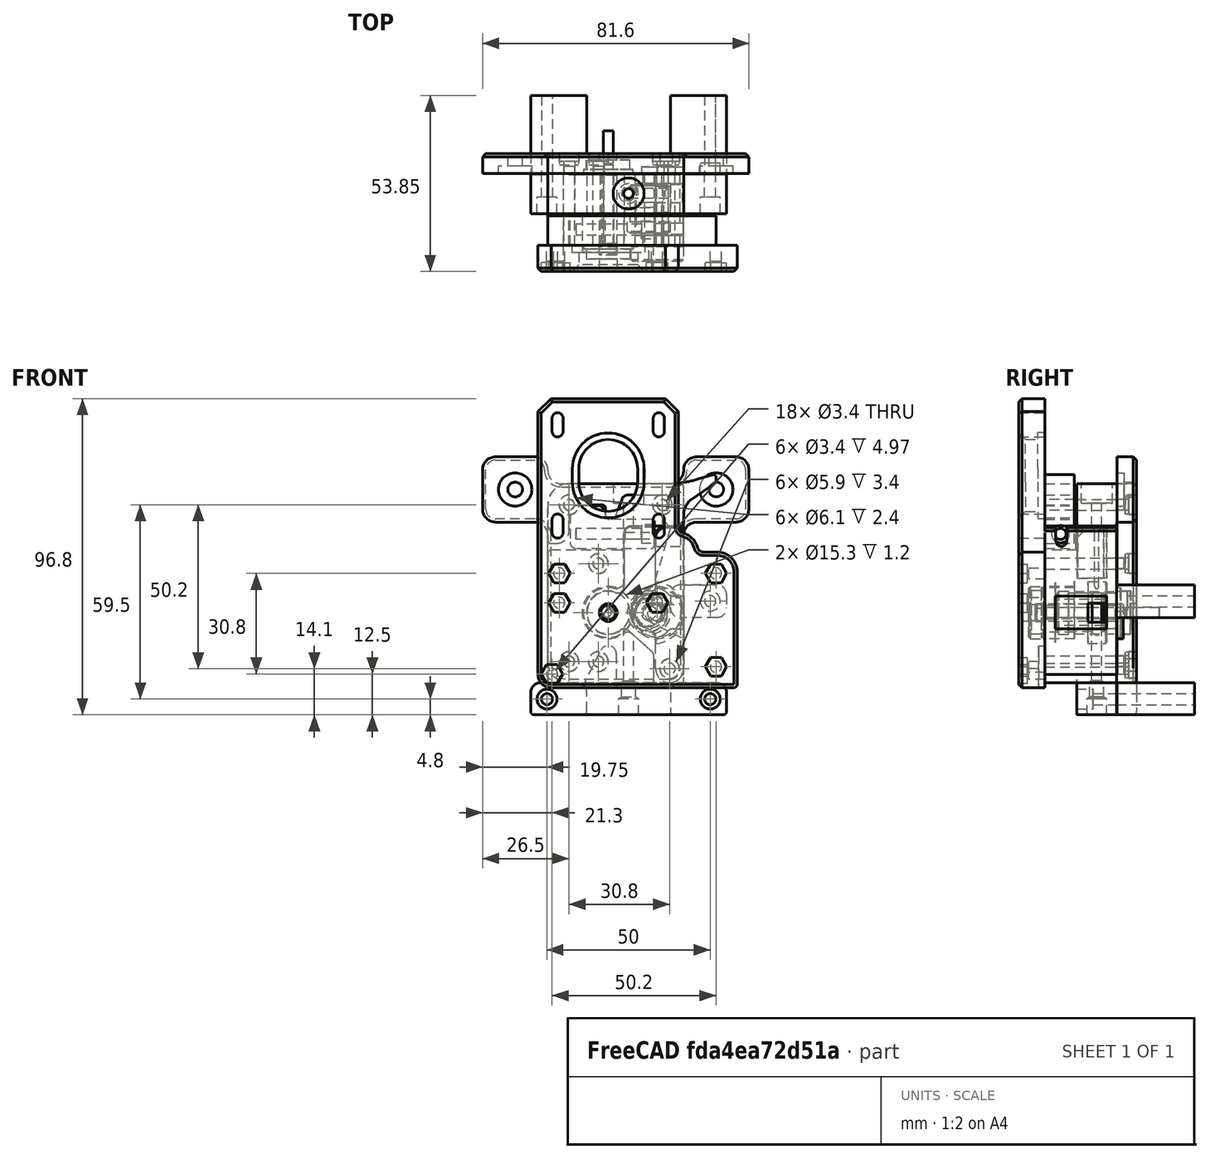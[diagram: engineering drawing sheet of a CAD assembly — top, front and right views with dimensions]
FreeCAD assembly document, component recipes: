
FREECAD ASSEMBLY — COMPONENT RECIPES ("belted_extruder_v0.4")

This assembly document has 4 components, labeled P0..P3 below (a component is one placed body or linked part). 4 of them carry a construction recipe — the FreeCAD feature program that regenerates the part from scratch, quoted from this document or its linked companion documents; the rest are supplied as boundary geometry only. No exploded tour is included for this assembly.
COMPONENT P0 — recipe-attached ("Extruder-BodyLower001", modeled in this document).
Construction recipe (the document's own serialized feature program — sketch geometry with constraints, then the solid features built on it; lengths are millimeters unless a unit is written):

FEATURE [PartDesign::SubShapeBinder] Binder009  label="Body Screw Binders"
  BindCopyOnChange = 0
  BindMode = 0
  ClaimChildren = false
  Context = -> Part005 [Body007.Binder009.]
  Fuse = false
  MakeFace = true
  OffsetFill = false
  OffsetIntersection = false
  OffsetJoinType = 0
  OffsetOpenResult = false
  PartialLoad = false
  Refine = true
  Relative = true
  Support = -> [Sketch014]
  _Version = 2
FEATURE [Sketcher::SketchObject] Sketch036  label="BaseSketch"
  ArcFitTolerance = 1e-06
  AttachmentOffset = pos=(0,0,-22) rot=(0,0,1;0rad)
  AttachmentSupport = -> [XZ_Plane028]
  ExternalGeometry = -> [Binder009]
  FullyConstrained = true
  MakeInternals = false
  MapMode = 5
  Placement = pos=(0,22,-4.9e-15) rot=(1,0,0;1.5708rad)
  sketch-geometry (22):
    g0: LineSegment StartX=-18.5 StartY=39.5 StartZ=0 EndX=-18.5 EndY=-21.5 EndZ=0
    g1: LineSegment [constr] StartX=-18.5 StartY=-21.5 StartZ=0 EndX=14 EndY=-21.5 EndZ=0
    g2: LineSegment StartX=14 StartY=-21.5 StartZ=0 EndX=14 EndY=-12.5 EndZ=0
    g3: ArcOfCircle CenterX=0 CenterY=0 CenterZ=0 NormalX=0 NormalY=0 NormalZ=1 AngleXU=0 Radius=6.5 StartAngle=0.720958 EndAngle=5.56223
    g4: Circle CenterX=-3 CenterY=15 CenterZ=0 NormalX=0 NormalY=0 NormalZ=1 AngleXU=0 Radius=1.7
    g5: Circle CenterX=-3 CenterY=-15 CenterZ=0 NormalX=0 NormalY=0 NormalZ=1 AngleXU=0 Radius=1.7
    g6: LineSegment [constr] StartX=4.88263 StartY=4.29068 StartZ=0 EndX=14 EndY=12.5 EndZ=0
    g7: LineSegment StartX=4.88263 StartY=-4.29068 StartZ=0 EndX=14 EndY=-12.5 EndZ=0
    g8: LineSegment [constr] StartX=14 StartY=12.5 StartZ=0 EndX=14 EndY=-12.5 EndZ=0
    g9: LineSegment [constr] StartX=4.88263 StartY=4.29068 StartZ=0 EndX=4.88263 EndY=-4.29068 EndZ=0
    g10: LineSegment StartX=23.1 StartY=39.5 StartZ=0 EndX=-18.5 EndY=39.5 EndZ=0
    g11: LineSegment StartX=4.88263 StartY=26.5 StartZ=0 EndX=23.1 EndY=26.5 EndZ=0
    g12: LineSegment StartX=23.1 StartY=26.5 StartZ=0 EndX=23.1 EndY=39.5 EndZ=0
    g13: LineSegment StartX=4.88263 StartY=26.5 StartZ=0 EndX=4.88263 EndY=4.29068 EndZ=0
    g14: Circle CenterX=16.6 CenterY=33 CenterZ=0 NormalX=0 NormalY=0 NormalZ=1 AngleXU=0 Radius=1.7
    g15: Circle CenterX=-12 CenterY=33 CenterZ=0 NormalX=0 NormalY=0 NormalZ=1 AngleXU=0 Radius=1.7
    g16: Circle CenterX=-12 CenterY=-15 CenterZ=0 NormalX=0 NormalY=0 NormalZ=1 AngleXU=0 Radius=1.7
    g17: LineSegment StartX=-18.5 StartY=-21.5 StartZ=0 EndX=-23.75 EndY=-21.5 EndZ=0
    g18: LineSegment StartX=-23.75 StartY=-21.5 StartZ=0 EndX=-23.75 EndY=-31.3 EndZ=0
    g19: LineSegment StartX=-23.75 StartY=-31.3 StartZ=0 EndX=36.25 EndY=-31.3 EndZ=0
    g20: LineSegment StartX=36.25 StartY=-31.3 StartZ=0 EndX=36.25 EndY=-21.5 EndZ=0
    g21: LineSegment StartX=36.25 StartY=-21.5 StartZ=0 EndX=14 EndY=-21.5 EndZ=0
  constraints (58):
    c: Coincident(g0,g1)
    c: Coincident(g1,g2)
    c: Coincident(g10,g0)
    c: Vertical(g0)
    c: Vertical(g2)
    c: Horizontal(g1)
    c: DistanceX(g0,g-3) = 6.5
    c: DistanceY(g0,g-4) = 6.5
    c: Coincident(g3,g-1)
    c: Diameter(g3) = 13
    c: DistanceY(g-3,g0) = 6.5
    c: Coincident(g4,g-5)
    c: Equal(g4,g-5)
    c: Coincident(g5,g-6)
    c: Equal(g5,g-6)
    c: DistanceY(g7,g6) = 25
    c: Symmetric(g6,g7,g-1)
    c: PointOnObject(g2,g7)
    c: Coincident(g8,g6)
    c: Coincident(g8,g2)
    c: Vertical(g8)
    c: Coincident(g7,g3)
    c: Coincident(g6,g3)
    c: Angle(g7,g6) = 1.46608
    c: Coincident(g9,g3)
    c: Coincident(g9,g3)
    c: Vertical(g9)
    c: Horizontal(g10)
    c: Horizontal(g11)
    c: Coincident(g12,g11)
    c: Vertical(g12)
    c: DistanceX(g3,g1) = 14
    c: Coincident(g13,g11)
    c: Vertical(g13)
    c: DistanceX(g-7,g12) = 6.5
    c: Coincident(g10,g12)
    c: DistanceY(g11,g-7) = 6.5
    c: Coincident(g13,g3)
    c: Coincident(g14,g-7)
    c: Equal(g14,g-7)
    c: Coincident(g15,g-3)
    c: Equal(g15,g-3)
    c: Coincident(g16,g-4)
    c: Equal(g16,g-4)
    c: Coincident(g0,g17)
    c: Horizontal(g17)
    c: Coincident(g17,g18)
    c: Vertical(g18)
    c: Coincident(g18,g19)
    c: Horizontal(g19)
    c: Coincident(g19,g20)
    c: Vertical(g20)
    c: Coincident(g20,g21)
    c: Coincident(g21,g1)
    c: Horizontal(g21)
    c: DistanceX(g19,g19) = 60
    c: DistanceY(g20,g20) = 9.8
    c: DistanceX(g17,g0) = 5.25
FEATURE [PartDesign::Pad] Pad008  label="Body Pad"
  Direction = (0,-1,2e-16)
  Length = 12.5
  Length2 = 10
  Placement = pos=(0,0,0) rot=(1,0,0;1.5708rad)
  Profile = -> Sketch036
  ReferenceAxis = -> Sketch036 [N_Axis]
  Refine = true
  Suppressed = false
  Type = 0
FEATURE [PartDesign::Fillet] Fillet021
  Base = -> Pad008 [Edge8]
  BaseFeature = -> Pad008
  Placement = pos=(0,0,0) rot=(1,0,0;1.5708rad)
  Radius = 6.5
  Refine = true
  SupportTransform = false
  Suppressed = false
  UseAllEdges = false
FEATURE [PartDesign::Fillet] Fillet022
  Base = -> Fillet021 [Edge50,Edge44]
  BaseFeature = -> Fillet021
  Placement = pos=(0,0,0) rot=(1,0,0;1.5708rad)
  Radius = 2
  Refine = true
  SupportTransform = false
  Suppressed = false
  UseAllEdges = false
FEATURE [PartDesign::SubShapeBinder] Binder010  label="Filament Path Binder"
  BindCopyOnChange = 0
  BindMode = 0
  ClaimChildren = false
  Context = -> Part005 [Body007.Binder010.]
  Fuse = false
  MakeFace = true
  OffsetFill = false
  OffsetIntersection = false
  OffsetJoinType = 0
  OffsetOpenResult = false
  PartialLoad = false
  Refine = true
  Relative = true
  Support = -> [Sketch006]
  _Version = 2
FEATURE [Sketcher::SketchObject] Sketch037
  ArcFitTolerance = 1e-06
  AttachmentSupport = -> [Pad008]
  ExternalGeometry = -> [Binder010]
  FullyConstrained = true
  MakeInternals = false
  MapMode = 5
  Placement = pos=(0,1.74e-14,39.5) rot=(0,0,1;3.14159rad)
  sketch-geometry (1):
    g0: Circle CenterX=-6.25 CenterY=-15.85 CenterZ=0 NormalX=0 NormalY=0 NormalZ=1 AngleXU=0 Radius=1.425
  constraints (2):
    c: Coincident(g0,g-3)
    c: Equal(g0,g-3)
FEATURE [Sketcher::SketchObject] Sketch038  label="Tensioner Latch Sketch"
  ArcFitTolerance = 1e-06
  FullyConstrained = true
  MakeInternals = false
  MapMode = 5
  Placement = pos=(23.1,0,0) rot=(0.707107,0,0.707107;3.14159rad)
  sketch-geometry (8):
    g0: LineSegment StartX=19.15 StartY=-9.7 StartZ=0 EndX=28.85 EndY=-9.7 EndZ=0
    g1: LineSegment StartX=28.85 StartY=-9.7 StartZ=0 EndX=28.85 EndY=0 EndZ=0
    g2: LineSegment StartX=28.85 StartY=0 StartZ=0 EndX=19.15 EndY=0 EndZ=0
    g3: LineSegment StartX=19.15 StartY=0 StartZ=0 EndX=19.15 EndY=-9.7 EndZ=0
    g4: Circle CenterX=24 CenterY=-4.85 CenterZ=0 NormalX=0 NormalY=0 NormalZ=1 AngleXU=0 Radius=2.75
    g5: LineSegment [constr] StartX=19.15 StartY=0 StartZ=0 EndX=28.85 EndY=-9.7 EndZ=0
    g6: LineSegment [constr] StartX=24 StartY=-9.7 StartZ=0 EndX=24 EndY=0 EndZ=0
    g7: LineSegment [constr] StartX=0 StartY=0 StartZ=0 EndX=19.15 EndY=0 EndZ=0
  constraints (20):
    c: Coincident(g0,g1)
    c: Coincident(g1,g2)
    c: Coincident(g2,g3)
    c: Coincident(g3,g0)
    c: Horizontal(g0)
    c: Horizontal(g2)
    c: Vertical(g1)
    c: Vertical(g3)
    c: Diameter(g4) = 5.5
    c: Coincident(g5,g2)
    c: Coincident(g5,g0)
    c: DistanceY(g1,g1) = 9.7
    c: Symmetric(g5,g5,g4)
    c: Equal(g2,g1)
    c: Symmetric(g0,g0,g6)
    c: Symmetric(g2,g2,g6)
    c: DistanceX(g-1,g6) = 24
    c: Coincident(g7,g-1)
    c: Coincident(g7,g2)
    c: Horizontal(g7)
FEATURE [PartDesign::Pocket] Pocket018  label="Tensioner Latch Cutout"
  BaseFeature = -> Fillet022
  Direction = (-1,1e-16,2e-16)
  Length = 0
  Length2 = 5
  Placement = pos=(0,0,0) rot=(1,0,0;1.5708rad)
  Profile = -> Sketch038
  ReferenceAxis = -> Sketch038 [N_Axis]
  Refine = true
  Suppressed = false
  Type = 3
  UpToFace = -> Fillet022 [Face10]
FEATURE [PartDesign::Pocket] Pocket019
  BaseFeature = -> Pocket018
  Direction = (0,1,0)
  Length = 0.2
  Length2 = 5
  Placement = pos=(0,0,0) rot=(1,0,0;1.5708rad)
  Profile = -> Pocket018 [Face24]
  Refine = true
  Suppressed = false
  Type = 0
FEATURE [PartDesign::Pad] Pad009
  BaseFeature = -> Pocket019
  Direction = (0,-1,0)
  Length = 9.5
  Length2 = 10
  Placement = pos=(0,0,0) rot=(1,0,0;1.5708rad)
  Profile = -> Pocket019 [Face23]
  Refine = true
  Suppressed = false
  Type = 0
FEATURE [Sketcher::SketchObject] Sketch039
  ArcFitTolerance = 1e-06
  AttachmentSupport = -> [Pad009]
  FullyConstrained = true
  MakeInternals = false
  MapMode = 5
  Placement = pos=(0,1.07e-14,0) rot=(1,0,0;1.5708rad)
  sketch-geometry (1):
    g0: Circle CenterX=0 CenterY=0 CenterZ=0 NormalX=0 NormalY=0 NormalZ=1 AngleXU=0 Radius=8
  constraints (2):
    c: Coincident(g0,g-1)
    c: Diameter(g0) = 16
FEATURE [PartDesign::Pocket] Pocket020
  BaseFeature = -> Pad009
  Direction = (0,1,-2e-16)
  Length = 9
  Length2 = 5
  Placement = pos=(0,0,0) rot=(1,0,0;1.5708rad)
  Profile = -> Sketch039
  ReferenceAxis = -> Sketch039 [N_Axis]
  Refine = true
  Suppressed = false
  Type = 0
FEATURE [PartDesign::Fillet] Fillet023
  Base = -> Pocket020 [Edge43,Edge31]
  BaseFeature = -> Pocket020
  Placement = pos=(0,0,0) rot=(1,0,0;1.5708rad)
  Radius = 2
  Refine = true
  SupportTransform = false
  Suppressed = false
  UseAllEdges = false
FEATURE [PartDesign::Fillet] Fillet024
  Base = -> Fillet023 [Edge46,Edge8]
  BaseFeature = -> Fillet023
  Placement = pos=(0,0,0) rot=(1,0,0;1.5708rad)
  Radius = 2
  Refine = true
  SupportTransform = false
  Suppressed = false
  UseAllEdges = false
FEATURE [PartDesign::Fillet] Fillet025  label="Sharp edges"
  Base = -> Fillet024 [Edge7,Edge72,Edge59,Edge73]
  BaseFeature = -> Fillet024
  Placement = pos=(0,0,0) rot=(1,0,0;1.5708rad)
  Radius = 1
  Refine = true
  SupportTransform = false
  Suppressed = false
  UseAllEdges = false
FEATURE [Sketcher::SketchObject] Sketch048  label="FilamentHole"
  ArcFitTolerance = 1e-06
  AttachmentSupport = -> [Fillet025]
  ExternalGeometry = -> [Binder010]
  FullyConstrained = true
  MakeInternals = false
  MapMode = 5
  Placement = pos=(0,-1.1e-14,-31.3) rot=(1,0,0;3.14159rad)
  sketch-geometry (1):
    g0: Circle CenterX=6.25 CenterY=-15.85 CenterZ=0 NormalX=0 NormalY=0 NormalZ=1 AngleXU=0 Radius=4.75
  constraints (2):
    c: Coincident(g0,g-3)
    c: Diameter(g0) = 9.5
FEATURE [Sketcher::SketchObject] Sketch049
  ArcFitTolerance = 1e-06
  ExternalGeometry = -> [Binder010]
  FullyConstrained = true
  MakeInternals = false
  MapMode = 5
  Placement = pos=(0,8.8e-15,39.5) rot=(0,0,1;3.14159rad)
  sketch-geometry (1):
    g0: Circle CenterX=-6.25 CenterY=-15.85 CenterZ=0 NormalX=0 NormalY=0 NormalZ=1 AngleXU=0 Radius=4.75
  constraints (2):
    c: Coincident(g0,g-3)
    c: Diameter(g0) = 9.5
FEATURE [PartDesign::Pocket] Pocket024  label="TopFilamentPath"
  BaseFeature = -> Fillet025
  Direction = (0,0,-1)
  Length = 6
  Length2 = 5
  Placement = pos=(0,0,0) rot=(1,0,0;1.5708rad)
  Profile = -> Sketch049
  ReferenceAxis = -> Sketch049 [N_Axis]
  Refine = true
  Suppressed = false
  Type = 0
FEATURE [PartDesign::Hole] Hole012  label="FilamentPathOut3mm"
  BaseFeature = -> Pocket024
  CustomThreadClearance = 0
  Depth = 100
  DepthType = 0
  Diameter = 3
  DrillForDepth = false
  DrillPoint = 1
  DrillPointAngle = 118
  HoleCutCountersinkAngle = 90
  HoleCutCustomValues = false
  HoleCutDepth = 0
  HoleCutDiameter = 6.1
  HoleCutType = 0
  ModelThread = false
  Placement = pos=(0,0,0) rot=(1,0,0;1.5708rad)
  Profile = -> Sketch048 [Edge1]
  Refine = true
  Suppressed = false
  Tapered = false
  TaperedAngle = 90
  ThreadClass = 0
  ThreadDepth = 100
  ThreadDepthType = 0
  ThreadDirection = 0
  ThreadFit = 0
  ThreadSize = 0
  ThreadType = 0
  Threaded = false
  UseCustomThreadClearance = false
FEATURE [PartDesign::Hole] Hole013  label="4mmPtfeHole"
  BaseFeature = -> Hole012
  CustomThreadClearance = 0
  Depth = 10
  DepthType = 0
  Diameter = 4.3
  DrillForDepth = false
  DrillPoint = 1
  DrillPointAngle = 118
  HoleCutCountersinkAngle = 90
  HoleCutCustomValues = false
  HoleCutDepth = 0
  HoleCutDiameter = 6.1
  HoleCutType = 0
  ModelThread = false
  Placement = pos=(0,0,0) rot=(1,0,0;1.5708rad)
  Profile = -> Hole012 [Edge116]
  Refine = true
  Reversed = true
  Suppressed = false
  Tapered = false
  TaperedAngle = 90
  ThreadClass = 0
  ThreadDepth = 10
  ThreadDepthType = 0
  ThreadDirection = 0
  ThreadFit = 0
  ThreadSize = 0
  ThreadType = 0
  Threaded = false
  UseCustomThreadClearance = false
FEATURE [PartDesign::Hole] Hole014  label="6mmPtfeHole"
  BaseFeature = -> Hole013
  CustomThreadClearance = 0
  Depth = 5
  DepthType = 0
  Diameter = 6
  DrillForDepth = false
  DrillPoint = 1
  DrillPointAngle = 118
  HoleCutCountersinkAngle = 90
  HoleCutCustomValues = false
  HoleCutDepth = 0
  HoleCutDiameter = 6.1
  HoleCutType = 0
  ModelThread = false
  Placement = pos=(0,0,0) rot=(1,0,0;1.5708rad)
  Profile = -> Hole013 [Edge116]
  Refine = true
  Reversed = true
  Suppressed = false
  Tapered = false
  TaperedAngle = 90
  ThreadClass = 0
  ThreadDepth = 5
  ThreadDepthType = 0
  ThreadDirection = 0
  ThreadFit = 0
  ThreadSize = 0
  ThreadType = 0
  Threaded = false
  UseCustomThreadClearance = false
FEATURE [Sketcher::SketchObject] Sketch069
  ArcFitTolerance = 1e-06
  AttachmentSupport = -> [Pocket024]
  ExternalGeometry = -> [Binder010,Sketch036,Hole014]
  FullyConstrained = true
  MakeInternals = false
  MapMode = 5
  Placement = pos=(0,-1.1e-14,-31.3) rot=(1,0,0;3.14159rad)
  sketch-geometry (6):
    g0: LineSegment [constr] StartX=36.25 StartY=-9.7 StartZ=0 EndX=-23.75 EndY=-9.7 EndZ=0
    g1: LineSegment [constr] StartX=6.25 StartY=-9.7 StartZ=0 EndX=6.25 EndY=-22 EndZ=0
    g2: LineSegment StartX=-23.75 StartY=0 StartZ=0 EndX=-23.75 EndY=-9.7 EndZ=0
    g3: LineSegment StartX=-23.75 StartY=-9.7 StartZ=0 EndX=36.25 EndY=-9.7 EndZ=0
    g4: LineSegment StartX=36.25 StartY=-9.7 StartZ=0 EndX=36.25 EndY=0 EndZ=0
    g5: LineSegment StartX=36.25 StartY=0 StartZ=0 EndX=-23.75 EndY=0 EndZ=0
  constraints (16):
    c: Horizontal(g0)
    c: Symmetric(g0,g0,g1)
    c: Symmetric(g1,g1,g-3)
    c: Vertical(g1)
    c: PointOnObject(g1,g-4)
    c: PointOnObject(g0,g-5)
    c: Coincident(g2,g3)
    c: Coincident(g3,g4)
    c: Coincident(g4,g5)
    c: Coincident(g5,g2)
    c: Vertical(g2)
    c: Vertical(g4)
    c: Horizontal(g3)
    c: Horizontal(g5)
    c: Coincident(g2,g-5)
    c: Coincident(g3,g0)
FEATURE [PartDesign::Pocket] Pocket037  label="SupportCutOut"
  BaseFeature = -> Hole014
  Direction = (0,0,1)
  Length = 0
  Length2 = 5
  Placement = pos=(0,0,0) rot=(1,0,0;1.5708rad)
  Profile = -> Sketch069
  ReferenceAxis = -> Sketch069 [N_Axis]
  Refine = true
  Suppressed = false
  Type = 3
  UpToFace = -> Hole014 [Face35]
FEATURE [Sketcher::SketchObject] Sketch070  label="MountHolesSk"
  ArcFitTolerance = 1e-06
  AttachmentSupport = -> [Pocket037]
  ExternalGeometry = -> [Fillet021]
  FullyConstrained = true
  MakeInternals = false
  MapMode = 5
  Placement = pos=(0,9.7,-2.1e-15) rot=(1,0,0;1.5708rad)
  sketch-geometry (4):
    g0: LineSegment [constr] StartX=-23.75 StartY=-26.5 StartZ=0 EndX=36.25 EndY=-26.5 EndZ=0
    g1: Circle CenterX=-18.75 CenterY=-26.5 CenterZ=0 NormalX=0 NormalY=0 NormalZ=1 AngleXU=0 Radius=1.6
    g2: Circle CenterX=31.25 CenterY=-26.5 CenterZ=0 NormalX=0 NormalY=0 NormalZ=1 AngleXU=0 Radius=1.6
    g3: GeomPoint [constr] X=6.25 Y=-26.5 Z=0
  constraints (10):
    c: PointOnObject(g1,g0)
    c: DistanceY(g0,g-3) = 5
    c: Diameter(g2) = 3.2
    c: Equal(g1,g2)
    c: DistanceX(g1,g2) = 50
    c: Symmetric(g0,g0,g3)
    c: Symmetric(g1,g2,g3)
    c: Horizontal(g0)
    c: PointOnObject(g0,g-3)
    c: PointOnObject(g0,g-4)
FEATURE [PartDesign::Hole] Hole015  label="MountHoles"
  BaseFeature = -> Pocket037
  CustomThreadClearance = 0
  Depth = 20
  DepthType = 0
  Diameter = 3.4
  DrillForDepth = false
  DrillPoint = 1
  DrillPointAngle = 118
  HoleCutCountersinkAngle = 90
  HoleCutCustomValues = false
  HoleCutDepth = 5
  HoleCutDiameter = 6.1
  HoleCutType = 1
  ModelThread = false
  Placement = pos=(0,0,0) rot=(1,0,0;1.5708rad)
  Profile = -> Sketch070
  Refine = true
  Suppressed = false
  Tapered = false
  TaperedAngle = 90
  ThreadClass = 0
  ThreadDepth = 20
  ThreadDepthType = 0
  ThreadDirection = 0
  ThreadFit = 0
  ThreadSize = 9
  ThreadType = 1
  Threaded = false
  UseCustomThreadClearance = false
FEATURE [PartDesign::Fillet] Fillet051
  Base = -> Hole015 [Edge119,Edge125]
  BaseFeature = -> Hole015
  Placement = pos=(0,0,0) rot=(1,0,0;1.5708rad)
  Radius = 3
  Refine = true
  SupportTransform = false
  Suppressed = false
  UseAllEdges = false
FEATURE [PartDesign::Fillet] Fillet052
  Base = -> Fillet051 [Edge46,Edge42,Edge37,Edge65]
  BaseFeature = -> Fillet051
  Placement = pos=(0,0,0) rot=(1,0,0;1.5708rad)
  Radius = 1
  Refine = true
  SupportTransform = false
  Suppressed = false
  UseAllEdges = false
FEATURE [PartDesign::Body] Body007  label="Body-Lower"
  AllowCompound = false
  Group = -> [Sketch036,Binder009,Pad008,Fillet021,Fillet022,Binder010,Sketch037,Sketch038,Pocket018,Pocket019,Pad009,Sketch039,Pocket020,Fillet023,Fillet024,Fillet025,Sketch048,Sketch049,Pocket024,Hole012,Hole013,Hole014,Sketch069,Pocket037,Sketch070,Hole015,Fillet051,Fillet052]
  Origin = -> Origin028
  Tip = -> Fillet052
COMPONENT P1 — recipe-attached ("Tensioner001", modeled in this document).
Construction recipe (the document's own serialized feature program — sketch geometry with constraints, then the solid features built on it; lengths are millimeters unless a unit is written):

FEATURE [PartDesign::SubShapeBinder] Binder003  label="filament path binder001"
  BindCopyOnChange = 0
  BindMode = 0
  ClaimChildren = false
  Context = -> Part003 [Body003.Binder003.]
  Fuse = false
  MakeFace = true
  OffsetFill = false
  OffsetIntersection = false
  OffsetJoinType = 0
  OffsetOpenResult = false
  PartialLoad = false
  Refine = true
  Relative = true
  Support = -> [Sketch006]
  _Version = 2
FEATURE [PartDesign::SubShapeBinder] Binder004  label="tensioner axel binder"
  BindCopyOnChange = 0
  BindMode = 0
  ClaimChildren = false
  Context = -> Part003 [Body003.Binder004.]
  Fuse = false
  MakeFace = true
  OffsetFill = false
  OffsetIntersection = false
  OffsetJoinType = 0
  OffsetOpenResult = false
  PartialLoad = false
  Refine = true
  Relative = true
  Support = -> [Sketch014]
  _Version = 2
FEATURE [Sketcher::SketchObject] Sketch013  label="tensioner base sketch"
  ArcFitTolerance = 1e-06
  AttachmentSupport = -> [XZ_Plane022]
  ExternalGeometry = -> [Binder004]
  FullyConstrained = true
  MakeInternals = false
  MapMode = 5
  Placement = pos=(0,0,0) rot=(1,0,0;1.5708rad)
  sketch-geometry (15):
    g0: Circle [constr] CenterX=12.7 CenterY=0 CenterZ=0 NormalX=0 NormalY=0 NormalZ=1 AngleXU=0 Radius=4.5
    g1: LineSegment StartX=14.55 StartY=4.5 StartZ=0 EndX=14.55 EndY=26 EndZ=0
    g2: LineSegment StartX=14.55 StartY=26 StartZ=0 EndX=23.05 EndY=26 EndZ=0
    g3: Circle CenterX=12.7 CenterY=0 CenterZ=0 NormalX=0 NormalY=0 NormalZ=1 AngleXU=0 Radius=2.1
    g4: LineSegment StartX=14.55 StartY=-17.2 StartZ=0 EndX=14.55 EndY=-6.2 EndZ=0
    g5: LineSegment StartX=23.05 StartY=26 StartZ=0 EndX=23.05 EndY=-17.2 EndZ=0
    g6: LineSegment StartX=10.4965 StartY=-3.92361 StartZ=0 EndX=14.55 EndY=-6.2 EndZ=0
    g7: LineSegment [constr] StartX=14.55 StartY=-6.2 StartZ=0 EndX=14.55 EndY=4.5 EndZ=0
    g8: LineSegment StartX=14.55 StartY=4.5 StartZ=0 EndX=12.7 EndY=4.5 EndZ=0
    g9: ArcOfCircle CenterX=12.7 CenterY=0 CenterZ=0 NormalX=0 NormalY=0 NormalZ=1 AngleXU=0 Radius=4.5 StartAngle=1.5708 EndAngle=4.20069
    g10: Circle [constr] CenterX=12.7 CenterY=0 CenterZ=0 NormalX=0 NormalY=0 NormalZ=1 AngleXU=0 Radius=6
    g11: ArcOfCircle CenterX=18.8 CenterY=-17.2 CenterZ=0 NormalX=0 NormalY=0 NormalZ=1 AngleXU=0 Radius=4.25 StartAngle=3.14159 EndAngle=5.49779
    g12: ArcOfCircle [constr] CenterX=18.8 CenterY=-17.2 CenterZ=0 NormalX=0 NormalY=0 NormalZ=1 AngleXU=0 Radius=4.25 StartAngle=5.49779 EndAngle=6.28319
    g13: LineSegment StartX=23.05 StartY=-18.9604 StartZ=0 EndX=21.8052 EndY=-20.2052 EndZ=0
    g14: LineSegment StartX=23.05 StartY=-18.9604 StartZ=0 EndX=23.05 EndY=-17.2 EndZ=0
  constraints (36):
    c: PointOnObject(g0,g-1)
    c: Diameter(g0) = 9
    c: Vertical(g1)
    c: Coincident(g1,g2)
    c: Horizontal(g2)
    c: Coincident(g3,g0)
    c: Diameter(g3) = 4.2
    c: DistanceX(g-1,g0) = 12.7
    c: Coincident(g-4,g11)
    c: Tangent(g11,g4) = 1.5708
    c: Coincident(g5,g2)
    c: Vertical(g5)
    c: Tangent(g12,g5) = 1.5708
    c: Coincident(g6,g4)
    c: Coincident(g7,g4)
    c: Coincident(g7,g1)
    c: Vertical(g7)
    c: Vertical(g4)
    c: Coincident(g8,g1)
    c: Tangent(g8,g0) = -1.5708
    c: Horizontal(g8)
    c: Coincident(g9,g0)
    c: Coincident(g9,g8)
    c: Diameter(g10) = 12
    c: Coincident(g10,g0)
    c: Tangent(g6,g9) = -1.5708
    c: DistanceY(g11,g4) = 11
    c: Coincident(g11,g12)
    c: Coincident(g11,g12)
    c: Diameter(g11) = 8.5
    c: Angle(g5,g13) = 2.35619
    c: Tangent(g13,g11) = 1.5708
    c: Coincident(g14,g13)
    c: Coincident(g14,g5)
    c: Vertical(g14)
    c: DistanceY(g1,g-3) = 7
FEATURE [PartDesign::Pad] Pad003  label="tensioner base"
  Direction = (0,-1,2e-16)
  Length = 22
  Length2 = 10
  Placement = pos=(0,0,0) rot=(1,0,0;1.5708rad)
  Profile = -> Sketch013
  ReferenceAxis = -> Sketch013 [N_Axis]
  Refine = true
  Reversed = true
  Suppressed = false
  Type = 0
FEATURE [Sketcher::SketchObject] Sketch015
  ArcFitTolerance = 1e-06
  AttachmentSupport = -> [Pad003]
  ExternalGeometry = -> [Pad003]
  FullyConstrained = true
  MakeInternals = false
  MapMode = 5
  Placement = pos=(0,22,0) rot=(-1,0,0;1.5708rad)
  sketch-geometry (4):
    g0: ArcOfCircle CenterX=12.7 CenterY=4.9e-15 CenterZ=0 NormalX=0 NormalY=0 NormalZ=1 AngleXU=0 Radius=8 StartAngle=0.675132 EndAngle=5.60805
    g1: LineSegment StartX=18.945 StartY=5 StartZ=0 EndX=23.05 EndY=5 EndZ=0
    g2: LineSegment StartX=18.945 StartY=-5 StartZ=0 EndX=23.05 EndY=-5 EndZ=0
    g3: LineSegment StartX=23.05 StartY=5 StartZ=0 EndX=23.05 EndY=-5 EndZ=0
  constraints (11):
    c: Coincident(g0,g-3)
    c: Diameter(g0) = 16
    c: Horizontal(g1)
    c: Horizontal(g2)
    c: Symmetric(g2,g1,g-1)
    c: DistanceY(g2,g1) = 10
    c: Coincident(g0,g1)
    c: Coincident(g0,g2)
    c: Coincident(g3,g1)
    c: Coincident(g3,g2)
    c: PointOnObject(g2,g-4)
FEATURE [PartDesign::Pocket] Pocket005  label="tensioner pulley cutout"
  BaseFeature = -> Pad003
  Direction = (0,-1,-2e-16)
  Length = 18.9
  Length2 = -3.1
  Placement = pos=(0,0,0) rot=(1,0,0;1.5708rad)
  Profile = -> Sketch015
  ReferenceAxis = -> Sketch015 [N_Axis]
  Refine = true
  Suppressed = false
  Type = 4
FEATURE [Sketcher::SketchObject] Sketch016  label="tensioner screw sketch"
  ArcFitTolerance = 1e-06
  AttachmentSupport = -> [Pocket005]
  FullyConstrained = true
  MakeInternals = false
  MapMode = 5
  Placement = pos=(23.05,0,0) rot=(0.707107,0,0.707107;3.14159rad)
  sketch-geometry (5):
    g0: ArcOfCircle CenterX=24 CenterY=-4.9 CenterZ=0 NormalX=0 NormalY=0 NormalZ=1 AngleXU=0 Radius=1.8 StartAngle=1.5708 EndAngle=4.71239
    g1: LineSegment StartX=24 StartY=-3.1 StartZ=0 EndX=30 EndY=-3.1 EndZ=0
    g2: LineSegment StartX=24 StartY=-6.7 StartZ=0 EndX=30 EndY=-6.7 EndZ=0
    g3: ArcOfCircle CenterX=30 CenterY=-4.9 CenterZ=0 NormalX=0 NormalY=0 NormalZ=1 AngleXU=0 Radius=1.8 StartAngle=4.71239 EndAngle=7.85398
    g4: LineSegment [constr] StartX=24 StartY=-4.9 StartZ=0 EndX=30 EndY=-4.9 EndZ=0
  constraints (14):
    c: Diameter(g0) = 3.6
    c: Horizontal(g2)
    c: Horizontal(g1)
    c: DistanceX(g-1,g0) = 24
    c: Coincident(g3,g1)
    c: Coincident(g3,g2)
    c: Coincident(g4,g0)
    c: Coincident(g4,g3)
    c: Horizontal(g4)
    c: Equal(g0,g3)
    c: Tangent(g0,g1) = 1.5708
    c: Tangent(g0,g2) = -1.5708
    c: DistanceX(g4,g4) = 6
    c: DistanceY(g3,g-1) = 4.9
FEATURE [Sketcher::SketchObject] Sketch017
  ArcFitTolerance = 1e-06
  ExternalGeometry = -> [Binder004]
  FullyConstrained = true
  MakeInternals = false
  MapMode = 5
  Placement = pos=(0,6e-16,0) rot=(1,0,0;1.5708rad)
  sketch-geometry (1):
    g0: Circle CenterX=18.8 CenterY=-17.2 CenterZ=0 NormalX=0 NormalY=0 NormalZ=1 AngleXU=0 Radius=1.7
  constraints (2):
    c: Coincident(g0,g-3)
    c: Equal(g0,g-3)
FEATURE [PartDesign::Hole] Hole003  label="tensioner axle"
  BaseFeature = -> Pocket005
  CustomThreadClearance = 0
  Depth = 25
  DepthType = 0
  Diameter = 3.4
  DrillForDepth = false
  DrillPoint = 1
  DrillPointAngle = 118
  HoleCutCountersinkAngle = 90
  HoleCutCustomValues = false
  HoleCutDepth = 0
  HoleCutDiameter = 6.1
  HoleCutType = 0
  ModelThread = false
  Placement = pos=(0,0,0) rot=(1,0,0;1.5708rad)
  Profile = -> Sketch017
  Refine = true
  Suppressed = false
  Tapered = false
  TaperedAngle = 90
  ThreadClass = 0
  ThreadDepth = 25
  ThreadDepthType = 0
  ThreadDirection = 0
  ThreadFit = 0
  ThreadSize = 0
  ThreadType = 0
  Threaded = false
  UseCustomThreadClearance = false
FEATURE [Sketcher::SketchObject] Sketch018
  ArcFitTolerance = 1e-06
  AttachmentSupport = -> [Hole003]
  ExternalGeometry = -> [Hole003]
  FullyConstrained = true
  MakeInternals = false
  MapMode = 5
  Placement = pos=(0,6e-16,0) rot=(1,0,0;1.5708rad)
  sketch-geometry (3):
    g0: LineSegment StartX=19.05 StartY=26 StartZ=0 EndX=14.55 EndY=10.5 EndZ=0
    g1: LineSegment StartX=14.55 StartY=10.5 StartZ=0 EndX=14.55 EndY=26 EndZ=0
    g2: LineSegment StartX=14.55 StartY=26 StartZ=0 EndX=19.05 EndY=26 EndZ=0
  constraints (8):
    c: PointOnObject(g0,g-4)
    c: PointOnObject(g0,g-3)
    c: DistanceX(g0,g-4) = 4
    c: DistanceY(g-3,g0) = 6
    c: Coincident(g1,g0)
    c: Coincident(g1,g-4)
    c: Coincident(g2,g1)
    c: Coincident(g2,g0)
FEATURE [PartDesign::Pocket] Pocket007  label="finger tab cutout"
  BaseFeature = -> Hole003
  Direction = (0,1,-2e-16)
  Length = 18
  Length2 = -10
  Placement = pos=(0,0,0) rot=(1,0,0;1.5708rad)
  Profile = -> Sketch018
  ReferenceAxis = -> Sketch018 [N_Axis]
  Refine = true
  Suppressed = false
  Type = 4
FEATURE [PartDesign::Fillet] Fillet026  label="tensioner clearance fillet"
  Base = -> Pocket007 [Edge26,Edge30]
  BaseFeature = -> Pocket007
  Placement = pos=(0,0,0) rot=(1,0,0;1.5708rad)
  Radius = 2
  Refine = true
  SupportTransform = false
  Suppressed = false
  UseAllEdges = false
FEATURE [PartDesign::Fillet] Fillet027  label="gear trunk fillet"
  Base = -> Fillet026 [Edge47,Edge18,Edge79,Edge64]
  BaseFeature = -> Fillet026
  Placement = pos=(0,0,0) rot=(1,0,0;1.5708rad)
  Radius = 2
  Refine = true
  SupportTransform = false
  Suppressed = false
  UseAllEdges = false
FEATURE [PartDesign::Fillet] Fillet028  label="axle tabs fillet"
  Base = -> Fillet027 [Edge91,Edge89,Edge4,Edge9]
  BaseFeature = -> Fillet027
  Placement = pos=(0,0,0) rot=(1,0,0;1.5708rad)
  Radius = 2
  Refine = true
  SupportTransform = false
  Suppressed = false
  UseAllEdges = false
FEATURE [Sketcher::SketchObject] Sketch051
  ArcFitTolerance = 1e-06
  AttachmentSupport = -> [Fillet028]
  ExternalGeometry = -> [Fillet028]
  FullyConstrained = true
  MakeInternals = false
  MapMode = 5
  Placement = pos=(23.05,0,0) rot=(0.707107,0,0.707107;3.14159rad)
  sketch-geometry (5):
    g0: ArcOfCircle CenterX=22 CenterY=-5 CenterZ=0 NormalX=0 NormalY=0 NormalZ=1 AngleXU=0 Radius=1.7 StartAngle=1.5708 EndAngle=4.71239
    g1: LineSegment StartX=22 StartY=-6.7 StartZ=0 EndX=26 EndY=-6.7 EndZ=0
    g2: LineSegment StartX=22 StartY=-3.3 StartZ=0 EndX=26 EndY=-3.3 EndZ=0
    g3: LineSegment [constr] StartX=22 StartY=-3.3 StartZ=0 EndX=22 EndY=-6.7 EndZ=0
    g4: LineSegment StartX=26 StartY=-3.3 StartZ=0 EndX=26 EndY=-6.7 EndZ=0
  constraints (13):
    c: Diameter(g0) = 3.4
    c: DistanceY(g0,g-1) = 5
    c: PointOnObject(g1,g-3)
    c: Horizontal(g1)
    c: PointOnObject(g2,g-3)
    c: Horizontal(g2)
    c: Tangent(g0,g1) = -1.5708
    c: Tangent(g0,g2) = 1.5708
    c: Coincident(g3,g0)
    c: Coincident(g3,g0)
    c: DistanceX(g-1,g0) = 22
    c: Coincident(g4,g2)
    c: Coincident(g4,g1)
FEATURE [PartDesign::Pocket] Pocket026
  BaseFeature = -> Fillet028
  Direction = (-1,0,2e-16)
  Length = 10
  Length2 = 5
  Placement = pos=(0,0,0) rot=(1,0,0;1.5708rad)
  Profile = -> Sketch051
  ReferenceAxis = -> Sketch051 [N_Axis]
  Refine = true
  Suppressed = false
  Type = 0
FEATURE [PartDesign::Chamfer] Chamfer013
  Angle = 45
  Base = -> Pocket026 [Edge98,Edge100]
  BaseFeature = -> Pocket026
  ChamferType = 0
  FlipDirection = false
  Placement = pos=(0,0,0) rot=(1,0,0;1.5708rad)
  Refine = true
  Size = 1
  Size2 = 1
  SupportTransform = false
  Suppressed = false
  UseAllEdges = false
FEATURE [PartDesign::Body] Body003  label="Tensioner Body"
  AllowCompound = false
  Group = -> [Binder003,Sketch013,Binder004,Pad003,Sketch015,Pocket005,Sketch016,Sketch017,Hole003,Sketch018,Pocket007,Fillet026,Fillet027,Fillet028,Sketch051,Pocket026,Chamfer013]
  Origin = -> Origin022
  Tip = -> Chamfer013
COMPONENT P2 — recipe-attached ("Tensioner-Latch001", modeled in this document).
Construction recipe (the document's own serialized feature program — sketch geometry with constraints, then the solid features built on it; lengths are millimeters unless a unit is written):

FEATURE [PartDesign::SubShapeBinder] Binder011  label="holes binder"
  BindCopyOnChange = 0
  BindMode = 0
  ClaimChildren = false
  Context = -> Part006 [Body008.Binder011.]
  Fuse = false
  MakeFace = true
  OffsetFill = false
  OffsetIntersection = false
  OffsetJoinType = 0
  OffsetOpenResult = false
  PartialLoad = false
  Refine = true
  Relative = true
  Support = -> [Sketch014]
  _Version = 2
FEATURE [Sketcher::SketchObject] Sketch040  label="Latch Base Sketch"
  ArcFitTolerance = 1e-06
  AttachmentSupport = -> [XZ_Plane030]
  ExternalGeometry = -> [Binder011]
  FullyConstrained = false
  MakeInternals = false
  MapMode = 5
  Placement = pos=(0,0,0) rot=(1,0,0;1.5708rad)
  sketch-geometry (25):
    g0: LineSegment StartX=-18.1 StartY=39.4 StartZ=0 EndX=-18.1 EndY=21.0678 EndZ=0
    g1: LineSegment StartX=23.5 StartY=39.4 StartZ=0 EndX=-18.1 EndY=39.4 EndZ=0
    g2: Circle [constr] CenterX=-11.6 CenterY=32.9 CenterZ=0 NormalX=0 NormalY=0 NormalZ=1 AngleXU=0 Radius=13.5
    g3: LineSegment StartX=-18.1 StartY=21.0678 StartZ=0 EndX=-11.6 EndY=21.0678 EndZ=0
    g4: LineSegment StartX=-11.6 StartY=21.0678 StartZ=0 EndX=-11.6 EndY=32.9 EndZ=0
    g5: LineSegment [constr] StartX=-11.6 StartY=32.9 StartZ=0 EndX=-18.1 EndY=21.0678 EndZ=0
    g6: LineSegment StartX=19 StartY=26.4 StartZ=0 EndX=23.5 EndY=26.4 EndZ=0
    g7: Circle [constr] CenterX=-11.6 CenterY=32.9 CenterZ=0 NormalX=0 NormalY=0 NormalZ=1 AngleXU=0 Radius=30.3
    g8: LineSegment StartX=23.5 StartY=26.4 StartZ=0 EndX=23.5 EndY=32.9 EndZ=0
    g9: LineSegment StartX=33.5 StartY=42.4992 StartZ=0 EndX=23.5 EndY=39.4 EndZ=0
    g10: LineSegment StartX=23.5 StartY=32.9 StartZ=0 EndX=33.4819 EndY=39.8062 EndZ=0
    g11: LineSegment StartX=33.4819 StartY=39.8062 StartZ=0 EndX=33.5 EndY=42.4992 EndZ=0
    g12: Circle [constr] CenterX=-11.6 CenterY=32.9 CenterZ=0 NormalX=0 NormalY=0 NormalZ=1 AngleXU=0 Radius=11.8322
    g13: LineSegment StartX=-11.6 StartY=32.9 StartZ=0 EndX=-0.464471 EndY=32.9 EndZ=0
    g14: LineSegment [constr] StartX=-0.464471 StartY=32.9 StartZ=0 EndX=17 EndY=32.9 EndZ=0
    g15: LineSegment StartX=-0.464471 StartY=32.9 StartZ=0 EndX=-0.464471 EndY=28.9 EndZ=0
    g16: LineSegment StartX=-0.464471 StartY=28.9 StartZ=0 EndX=2.53553 EndY=28.9 EndZ=0
    g17: LineSegment StartX=2.53553 StartY=28.9 StartZ=0 EndX=5.08332 EndY=35.9 EndZ=0
    g18: LineSegment StartX=5.08332 StartY=35.9 StartZ=0 EndX=19 EndY=35.9 EndZ=0
    g19: LineSegment StartX=19 StartY=35.9 StartZ=0 EndX=19 EndY=31.2 EndZ=0
    g20: LineSegment StartX=17 StartY=31.2 StartZ=0 EndX=19 EndY=31.2 EndZ=0
    g21: LineSegment [constr] StartX=23.5 StartY=39.4 StartZ=0 EndX=23.5 EndY=32.9 EndZ=0
    g22: LineSegment StartX=17 StartY=31.2 StartZ=0 EndX=17 EndY=28.4 EndZ=0
    g23: LineSegment StartX=17 StartY=28.4 StartZ=0 EndX=19 EndY=26.4 EndZ=0
    g24: LineSegment [constr] StartX=19 StartY=31.2 StartZ=0 EndX=19 EndY=26.4 EndZ=0
  constraints (62):
    c: Coincident(g0,g3)
    c: Coincident(g6,g8)
    c: Coincident(g9,g1)
    c: Coincident(g1,g0)
    c: Vertical(g0)
    c: Horizontal(g1)
    c: DistanceY(g-3,g0) = 6.5
    c: DistanceX(g-4,g9) = 6.5
    c: Coincident(g2,g-3)
    c: Diameter(g2) = 27
    c: Coincident(g3,g4)
    c: Horizontal(g3)
    c: Coincident(g4,g13)
    c: DistanceX(g0,g2) = 6.5
    c: Coincident(g5,g2)
    c: Coincident(g5,g0)
    c: Distance(g5,g5) = 13.5
    c: DistanceY(g8,g-4) = 6.5
    c: Coincident(g23,g6)
    c: Horizontal(g6)
    c: Coincident(g4,g2)
    c: Coincident(g14,g-4)
    c: Coincident(g7,g2)
    c: Tangent(g7,g-4)
    c: Coincident(g8,g10)
    c: Vertical(g8)
    c: Coincident(g11,g9)
    c: Coincident(g10,g11)
    c: Coincident(g12,g2)
    c: Tangent(g3,g12) = -1.5708
    c: Coincident(g13,g14)
    c: Coincident(g13,g15)
    c: PointOnObject(g15,g12)
    c: Coincident(g15,g16)
    c: Horizontal(g16)
    c: Coincident(g16,g17)
    c: Coincident(g17,g18)
    c: Horizontal(g18)
    c: DistanceY(g15,g13) = 4
    c: DistanceX(g16,g16) = 3
    c: Coincident(g18,g19)
    c: Vertical(g19)
    c: Coincident(g20,g19)
    c: Coincident(g21,g1)
    c: Coincident(g21,g8)
    c: Horizontal(g20)
    c: Coincident(g22,g23)
    c: Vertical(g22)
    c: Coincident(g20,g22)
    c: DistanceX(g14,g18) = 2
    c: DistanceX(g20,g20) = 2
    c: Angle(g17,g18) = 1.91986
    c: Horizontal(g14)
    c: Vertical(g15)
    c: DistanceY(g18,g1) = 3.5
    c: DistanceY(g19,g19) = 4.7
    c: Coincident(g24,g19)
    c: Coincident(g24,g6)
    c: Vertical(g24)
    c: Angle(g24,g23) = 0.785398
    c: DistanceX(g1,g9) = 10
    c: Symmetric(g1,g6,g8)
FEATURE [PartDesign::Pad] Pad010
  Direction = (0,-1,2e-16)
  Length = 9
  Length2 = 10
  Placement = pos=(0,0,0) rot=(1,0,0;1.5708rad)
  Profile = -> Sketch040
  ReferenceAxis = -> Sketch040 [N_Axis]
  Refine = true
  Reversed = true
  Suppressed = false
  Type = 0
FEATURE [PartDesign::Fillet] Fillet029  label="Large Corner"
  Base = -> Pad010 [Edge23]
  BaseFeature = -> Pad010
  Placement = pos=(0,0,0) rot=(1,0,0;1.5708rad)
  Radius = 6.5
  Refine = true
  SupportTransform = false
  Suppressed = false
  UseAllEdges = false
FEATURE [PartDesign::Fillet] Fillet030  label="Large Cam"
  Base = -> Fillet029 [Edge45]
  BaseFeature = -> Fillet029
  Placement = pos=(0,0,0) rot=(1,0,0;1.5708rad)
  Radius = 4
  Refine = true
  SupportTransform = false
  Suppressed = false
  UseAllEdges = false
FEATURE [PartDesign::Fillet] Fillet031  label="Small Cam"
  Base = -> Fillet030 [Edge36]
  BaseFeature = -> Fillet030
  Placement = pos=(0,0,0) rot=(1,0,0;1.5708rad)
  Radius = 1
  Refine = true
  SupportTransform = false
  Suppressed = false
  UseAllEdges = false
FEATURE [PartDesign::Fillet] Fillet032  label="Small Printability"
  Base = -> Fillet031 [Edge23,Edge37,Edge29,Edge57,Edge53,Edge39,Edge41]
  BaseFeature = -> Fillet031
  Placement = pos=(0,0,0) rot=(1,0,0;1.5708rad)
  Radius = 1
  Refine = true
  SupportTransform = false
  Suppressed = false
  UseAllEdges = false
FEATURE [PartDesign::Fillet] Fillet033  label="Large Strain Relief"
  Base = -> Fillet032 [Edge46]
  BaseFeature = -> Fillet032
  Placement = pos=(0,0,0) rot=(1,0,0;1.5708rad)
  Radius = 2
  Refine = true
  SupportTransform = false
  Suppressed = false
  UseAllEdges = false
FEATURE [PartDesign::Fillet] Fillet034  label="Clasp"
  Base = -> Fillet033 [Edge57]
  BaseFeature = -> Fillet033
  Placement = pos=(0,0,0) rot=(1,0,0;1.5708rad)
  Radius = 4
  Refine = true
  SupportTransform = false
  Suppressed = false
  UseAllEdges = false
FEATURE [Sketcher::SketchObject] Sketch043
  ArcFitTolerance = 1e-06
  AttachmentSupport = -> [Fillet033]
  ExternalGeometry = -> [Binder011]
  FullyConstrained = true
  MakeInternals = false
  MapMode = 5
  Placement = pos=(0,1e-16,0) rot=(1,0,0;1.5708rad)
  sketch-geometry (1):
    g0: Circle CenterX=-11.6 CenterY=32.9 CenterZ=0 NormalX=0 NormalY=0 NormalZ=1 AngleXU=0 Radius=1.7
  constraints (2):
    c: Coincident(g0,g-3)
    c: Equal(g0,g-3)
FEATURE [PartDesign::Pocket] Pocket021
  BaseFeature = -> Fillet034
  Direction = (0,1,-2e-16)
  Length = 9
  Length2 = 5
  Placement = pos=(0,0,0) rot=(1,0,0;1.5708rad)
  Profile = -> Sketch043
  ReferenceAxis = -> Sketch043 [N_Axis]
  Refine = true
  Suppressed = false
  Type = 0
FEATURE [PartDesign::Fillet] Fillet040
  Base = -> Pocket021 [Edge43]
  BaseFeature = -> Pocket021
  Placement = pos=(0,0,0) rot=(1,0,0;1.5708rad)
  Radius = 6
  Refine = true
  SupportTransform = false
  Suppressed = false
  UseAllEdges = false
FEATURE [PartDesign::Fillet] Fillet041
  Base = -> Fillet040 [Edge48]
  BaseFeature = -> Fillet040
  Placement = pos=(0,0,0) rot=(1,0,0;1.5708rad)
  Radius = 32
  Refine = true
  SupportTransform = false
  Suppressed = false
  UseAllEdges = false
FEATURE [PartDesign::Fillet] Fillet042
  Base = -> Fillet041 [Edge39,Edge35]
  BaseFeature = -> Fillet041
  Placement = pos=(0,0,0) rot=(1,0,0;1.5708rad)
  Radius = 1
  Refine = true
  SupportTransform = false
  Suppressed = false
  UseAllEdges = false
FEATURE [PartDesign::Body] Body008  label="Latch-Body008"
  AllowCompound = false
  Group = -> [Binder011,Sketch040,Pad010,Fillet029,Fillet030,Fillet031,Fillet032,Fillet033,Fillet034,Sketch043,Pocket021,Fillet040,Fillet041,Fillet042]
  Origin = -> Origin030
  Placement = pos=(-0.4,0,0.1) rot=(0,0,1;0rad)
  Tip = -> Fillet042
COMPONENT P3 — recipe-attached ("Tensioner Shuttle001", modeled in this document).
Construction recipe (the document's own serialized feature program — sketch geometry with constraints, then the solid features built on it; lengths are millimeters unless a unit is written):

FEATURE [Sketcher::SketchObject] Sketch042
  ArcFitTolerance = 1e-06
  AttachmentSupport = -> [XZ_Plane033]
  FullyConstrained = false
  MakeInternals = false
  MapMode = 5
  Placement = pos=(0,0,0) rot=(1,0,0;1.5708rad)
  sketch-geometry (8):
    g0: LineSegment StartX=-11.6782 StartY=19.6096 StartZ=0 EndX=14.1697 EndY=19.6096 EndZ=0
    g1: LineSegment StartX=14.1697 StartY=19.6096 StartZ=0 EndX=14.1697 EndY=28.5688 EndZ=0
    g2: LineSegment StartX=-11.6782 StartY=32.7888 StartZ=0 EndX=-11.6782 EndY=19.6096 EndZ=0
    g3: LineSegment StartX=-2.60034 StartY=32.7888 StartZ=0 EndX=-11.6782 EndY=32.7888 EndZ=0
    g4: LineSegment StartX=14.1697 StartY=28.5688 StartZ=0 EndX=0.426484 EndY=28.5688 EndZ=0
    g5: ArcOfCircle CenterX=0.426484 CenterY=29.8688 CenterZ=0 NormalX=0 NormalY=0 NormalZ=1 AngleXU=0 Radius=1.3 StartAngle=3.15779 EndAngle=4.71239
    g6: GeomPoint [constr] X=-0.880539 Y=28.5688 Z=0
    g7: ArcOfCircle CenterX=-4.33667 CenterY=29.7916 CenterZ=0 NormalX=0 NormalY=0 NormalZ=1 AngleXU=0 Radius=3.46378 StartAngle=0.0161965 EndAngle=1.04572
  constraints (16):
    c: Coincident(g0,g1)
    c: Coincident(g1,g4)
    c: Coincident(g3,g2)
    c: Coincident(g2,g0)
    c: Horizontal(g0)
    c: Vertical(g1)
    c: Vertical(g2)
    c: Horizontal(g3)
    c: Horizontal(g4)
    c: PointOnObject(g6,g4)
    c: Tangent(g4,g5) = 1.5708
    c: Block(g1)
    c: Radius(g5) = 1.3
    c: Coincident(g3,g7)
    c: Tangent(g5,g7) = 1.5708
    c: DistanceY(g4,g3) = 4.22
FEATURE [PartDesign::Pad] Pad011
  Direction = (0,-1,2e-16)
  Length = 9.5
  Length2 = 10
  Placement = pos=(0,0,0) rot=(1,0,0;1.5708rad)
  Profile = -> Sketch042
  ReferenceAxis = -> Sketch042 [N_Axis]
  Refine = true
  Reversed = true
  Suppressed = false
  Type = 0
FEATURE [PartDesign::Fillet] Fillet035
  Base = -> Pad011 [Edge17]
  BaseFeature = -> Pad011
  Placement = pos=(0,0,0) rot=(1,0,0;1.5708rad)
  Radius = 2.5
  Refine = true
  SupportTransform = false
  Suppressed = false
  UseAllEdges = false
FEATURE [Sketcher::SketchObject] Sketch052
  ArcFitTolerance = 1e-06
  AttachmentSupport = -> [Fillet035]
  ExternalGeometry = -> [Fillet035]
  FullyConstrained = true
  MakeInternals = false
  MapMode = 5
  Placement = pos=(14.1697,0,0) rot=(0.707107,0,0.707107;3.14159rad)
  expr: Constraints[0] = <<Dimensions>>.M3HeatSetW
  sketch-geometry (3):
    g0: Circle CenterX=24.0892 CenterY=-4.75 CenterZ=0 NormalX=0 NormalY=0 NormalZ=1 AngleXU=0 Radius=2.75
    g1: LineSegment [constr] StartX=19.6096 StartY=-4.75 StartZ=0 EndX=24.0892 EndY=-4.75 EndZ=0
    g2: LineSegment [constr] StartX=24.0892 StartY=-9.5 StartZ=0 EndX=24.0892 EndY=-4.75 EndZ=0
  constraints (7):
    c: Diameter(g0) = 5.5
    c: Symmetric(g-4,g-4,g1)
    c: Coincident(g1,g0)
    c: Symmetric(g-3,g-3,g2)
    c: Coincident(g2,g0)
    c: Vertical(g2)
    c: Horizontal(g1)
FEATURE [PartDesign::Pocket] Pocket027
  BaseFeature = -> Fillet035
  Direction = (-1,0,2e-16)
  Length = 4
  Length2 = 5
  Placement = pos=(0,0,0) rot=(1,0,0;1.5708rad)
  Profile = -> Sketch052
  ReferenceAxis = -> Sketch052 [N_Axis]
  Refine = true
  Suppressed = false
  Type = 0
  expr: Length = <<Dimensions>>.M3HeatSetD
FEATURE [PartDesign::Fillet] Fillet043
  Base = -> Pocket027 [Edge24,Edge23]
  BaseFeature = -> Pocket027
  Placement = pos=(0,0,0) rot=(1,0,0;1.5708rad)
  Radius = 1
  Refine = true
  SupportTransform = false
  Suppressed = false
  UseAllEdges = false
FEATURE [PartDesign::Fillet] Fillet044
  Base = -> Fillet043 [Edge12]
  BaseFeature = -> Fillet043
  Placement = pos=(0,0,0) rot=(1,0,0;1.5708rad)
  Radius = 2
  Refine = true
  SupportTransform = false
  Suppressed = false
  UseAllEdges = false
FEATURE [PartDesign::Hole] Hole010
  BaseFeature = -> Fillet044
  CustomThreadClearance = 0
  Depth = 20
  DepthType = 0
  Diameter = 3.4
  DrillForDepth = false
  DrillPoint = 0
  DrillPointAngle = 118
  HoleCutCountersinkAngle = 90
  HoleCutCustomValues = false
  HoleCutDepth = 0
  HoleCutDiameter = 6.1
  HoleCutType = 0
  ModelThread = false
  Placement = pos=(0,0,0) rot=(1,0,0;1.5708rad)
  Profile = -> Fillet044 [Edge36]
  Refine = true
  Suppressed = false
  Tapered = false
  TaperedAngle = 90
  ThreadClass = 0
  ThreadDepth = 20
  ThreadDepthType = 0
  ThreadDirection = 0
  ThreadFit = 0
  ThreadSize = 9
  ThreadType = 1
  Threaded = false
  UseCustomThreadClearance = false
FEATURE [Sketcher::SketchObject] Sketch053
  ArcFitTolerance = 1e-06
  AttachmentSupport = -> [Hole010]
  ExternalGeometry = -> [Hole010]
  FullyConstrained = true
  MakeInternals = false
  MapMode = 5
  Placement = pos=(0,9.5,0) rot=(-1,0,0;1.5708rad)
  sketch-geometry (4):
    g0: LineSegment StartX=14.1697 StartY=-26.1096 StartZ=0 EndX=5.16969 EndY=-26.1096 EndZ=0
    g1: LineSegment StartX=5.16969 StartY=-26.1096 StartZ=0 EndX=5.16969 EndY=-22.6096 EndZ=0
    g2: LineSegment StartX=5.16969 StartY=-22.6096 StartZ=0 EndX=14.1697 EndY=-22.6096 EndZ=0
    g3: LineSegment StartX=14.1697 StartY=-22.6096 StartZ=0 EndX=14.1697 EndY=-26.1096 EndZ=0
  constraints (12):
    c: PointOnObject(g0,g-3)
    c: Horizontal(g0)
    c: Coincident(g0,g1)
    c: Vertical(g1)
    c: Coincident(g1,g2)
    c: PointOnObject(g2,g-3)
    c: Horizontal(g2)
    c: Coincident(g2,g3)
    c: Coincident(g3,g0)
    c: DistanceY(g3,g3) = 3.5
    c: DistanceX(g2,g2) = 9
    c: DistanceY(g2,g-4) = 3
FEATURE [PartDesign::Pad] Pad015
  BaseFeature = -> Hole010
  Direction = (0,1,2e-16)
  Length = 2
  Length2 = 10
  Placement = pos=(0,0,0) rot=(1,0,0;1.5708rad)
  Profile = -> Sketch053
  ReferenceAxis = -> Sketch053 [N_Axis]
  Refine = true
  Suppressed = false
  Type = 0
FEATURE [PartDesign::Fillet] Fillet045
  Base = -> Pad015 [Edge41]
  BaseFeature = -> Pad015
  Placement = pos=(0,0,0) rot=(1,0,0;1.5708rad)
  Radius = 1.5
  Refine = true
  SupportTransform = false
  Suppressed = false
  UseAllEdges = false
FEATURE [PartDesign::Chamfer] Chamfer014
  Angle = 45
  Base = -> Fillet045 [Edge23]
  BaseFeature = -> Fillet045
  ChamferType = 0
  FlipDirection = false
  Placement = pos=(0,0,0) rot=(1,0,0;1.5708rad)
  Refine = true
  Size = 1.98
  Size2 = 1
  SupportTransform = false
  Suppressed = false
  UseAllEdges = false
FEATURE [PartDesign::Body] Body009
  AllowCompound = false
  Group = -> [Sketch042,Pad011,Fillet035,Sketch052,Pocket027,Fillet043,Fillet044,Hole010,Sketch053,Pad015,Fillet045,Chamfer014]
  Origin = -> Origin033
  Tip = -> Chamfer014
PROVENANCE & LICENSES
A FreeCAD (.FCStd) document from a public repository crawl; recipes are the document's own serialized feature recipes (and, for linked parts, companion documents' recipes).
License: gpl-3.0.
